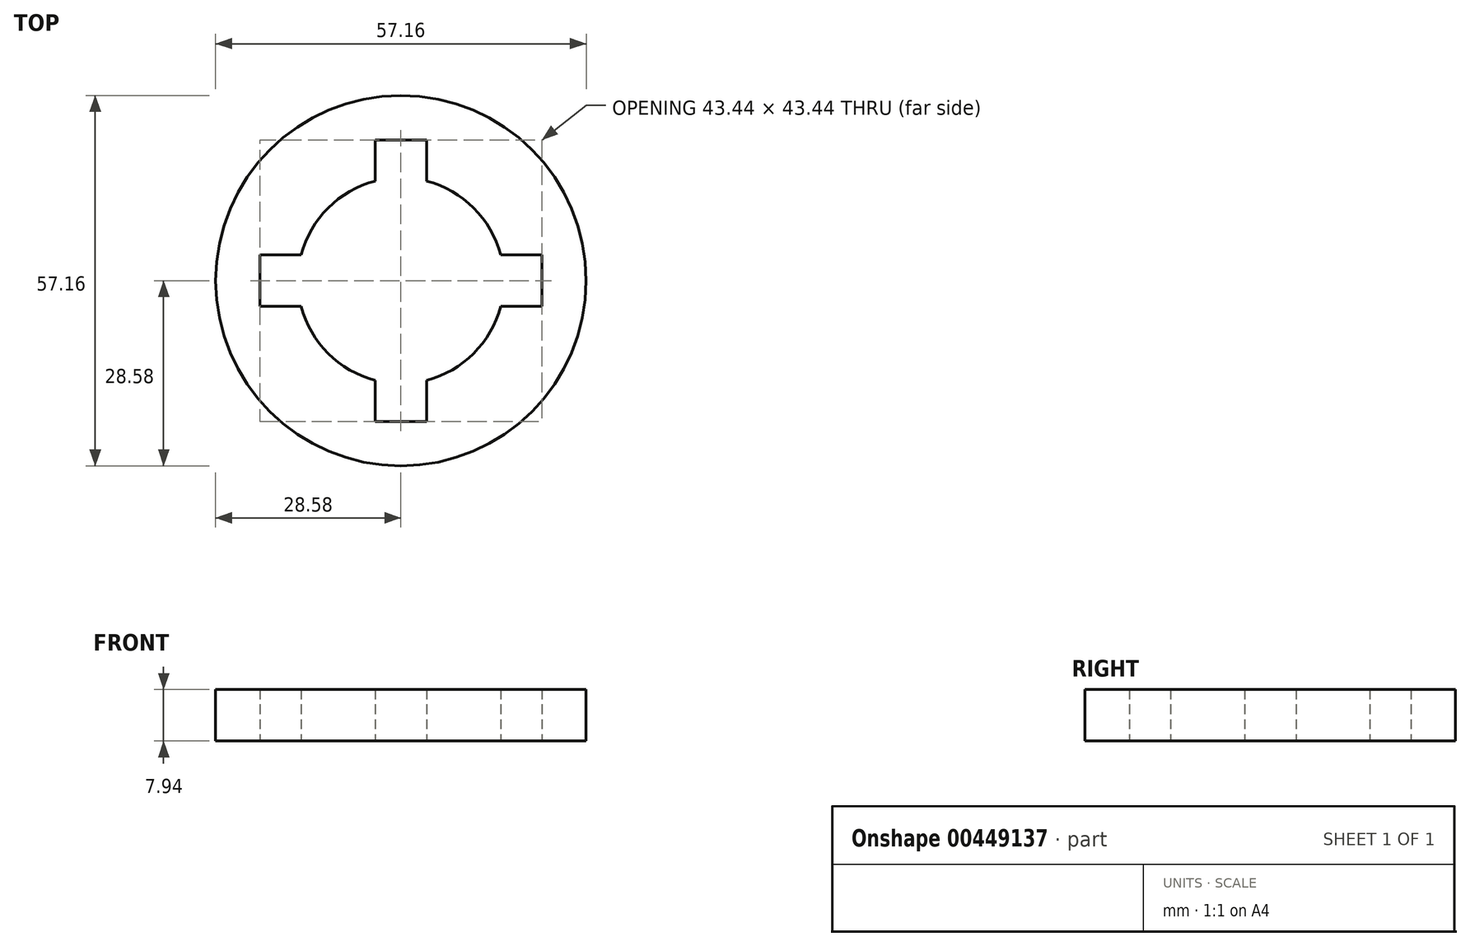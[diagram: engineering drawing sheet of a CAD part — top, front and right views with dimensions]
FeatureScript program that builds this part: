
annotation { "Feature Type Name" : "Feature", "Feature Type Description" : "" }
export const myFeature = defineFeature(function(context is Context, id is Id, definition is map)
    precondition{}
    {
        {
            var Q0;
            Q0=qCreatedBy(makeId("Top.planeOp"),FACE);
            var sketch = newSketch(context, id + "F0", { "sketchPlane" : qUnion([Q0])});
            skCircle(sketch, "E0", {"center": v(0, 0) * mm, "radius": 15.88 * mm});
            skCircle(sketch, "E1", {"center": v(0, 0) * mm, "radius": 28.58 * mm});
            skLineSegment(sketch, "E2.bottom", {"start": v(-15.37, 3.97) * mm, "end": v(-21.72, 3.97) * mm});
            skLineSegment(sketch, "E2.top", {"start": v(-15.37, -3.97) * mm, "end": v(-21.72, -3.97) * mm});
            skLineSegment(sketch, "E2.left", {"start": v(-15.37, 3.97) * mm, "end": v(-15.37, -3.97) * mm});
            skLineSegment(sketch, "E2.right", {"start": v(-21.72, 3.97) * mm, "end": v(-21.72, -3.97) * mm});
            skPoint(sketch, "E2.middle", {"position": v(-18.55, 0) * mm});
            skLineSegment(sketch, "E3.bottom", {"start": v(3.97, 15.37) * mm, "end": v(-3.97, 15.37) * mm});
            skLineSegment(sketch, "E3.top", {"start": v(3.97, 21.72) * mm, "end": v(-3.97, 21.72) * mm});
            skLineSegment(sketch, "E3.left", {"start": v(3.97, 15.37) * mm, "end": v(3.97, 21.72) * mm});
            skLineSegment(sketch, "E3.right", {"start": v(-3.97, 15.37) * mm, "end": v(-3.97, 21.72) * mm});
            skPoint(sketch, "E3.middle", {"position": v(0, 18.55) * mm});
            skLineSegment(sketch, "E4.bottom", {"start": v(-3.97, -15.37) * mm, "end": v(3.97, -15.37) * mm});
            skLineSegment(sketch, "E4.top", {"start": v(-3.97, -21.72) * mm, "end": v(3.97, -21.72) * mm});
            skLineSegment(sketch, "E4.left", {"start": v(-3.97, -15.37) * mm, "end": v(-3.97, -21.72) * mm});
            skLineSegment(sketch, "E4.right", {"start": v(3.97, -15.37) * mm, "end": v(3.97, -21.72) * mm});
            skPoint(sketch, "E4.middle", {"position": v(0, -18.55) * mm});
            skLineSegment(sketch, "E5.bottom", {"start": v(15.37, -3.97) * mm, "end": v(21.72, -3.97) * mm});
            skLineSegment(sketch, "E5.top", {"start": v(15.37, 3.97) * mm, "end": v(21.72, 3.97) * mm});
            skLineSegment(sketch, "E5.left", {"start": v(15.37, -3.97) * mm, "end": v(15.37, 3.97) * mm});
            skLineSegment(sketch, "E5.right", {"start": v(21.72, -3.97) * mm, "end": v(21.72, 3.97) * mm});
            skPoint(sketch, "E5.middle", {"position": v(18.55, 0) * mm});
            skSolve(sketch);
        }
        {
            var Q0;
            Q0=makeQuery(id+"F0.imprint","IMPRINT",FACE,{"disambiguationData":[TD([[makeQuery(id+"F0.imprint","IMPRINT",EDGE,{"derivedFrom":sQuery(id+"F0.wireOp",EDGE,"E1")}),1.0]])]});
            extrude(context, id + "F1", {"entities" : qUnion([Q0]), "depth" : 7.94 * mm});
        }
    });
